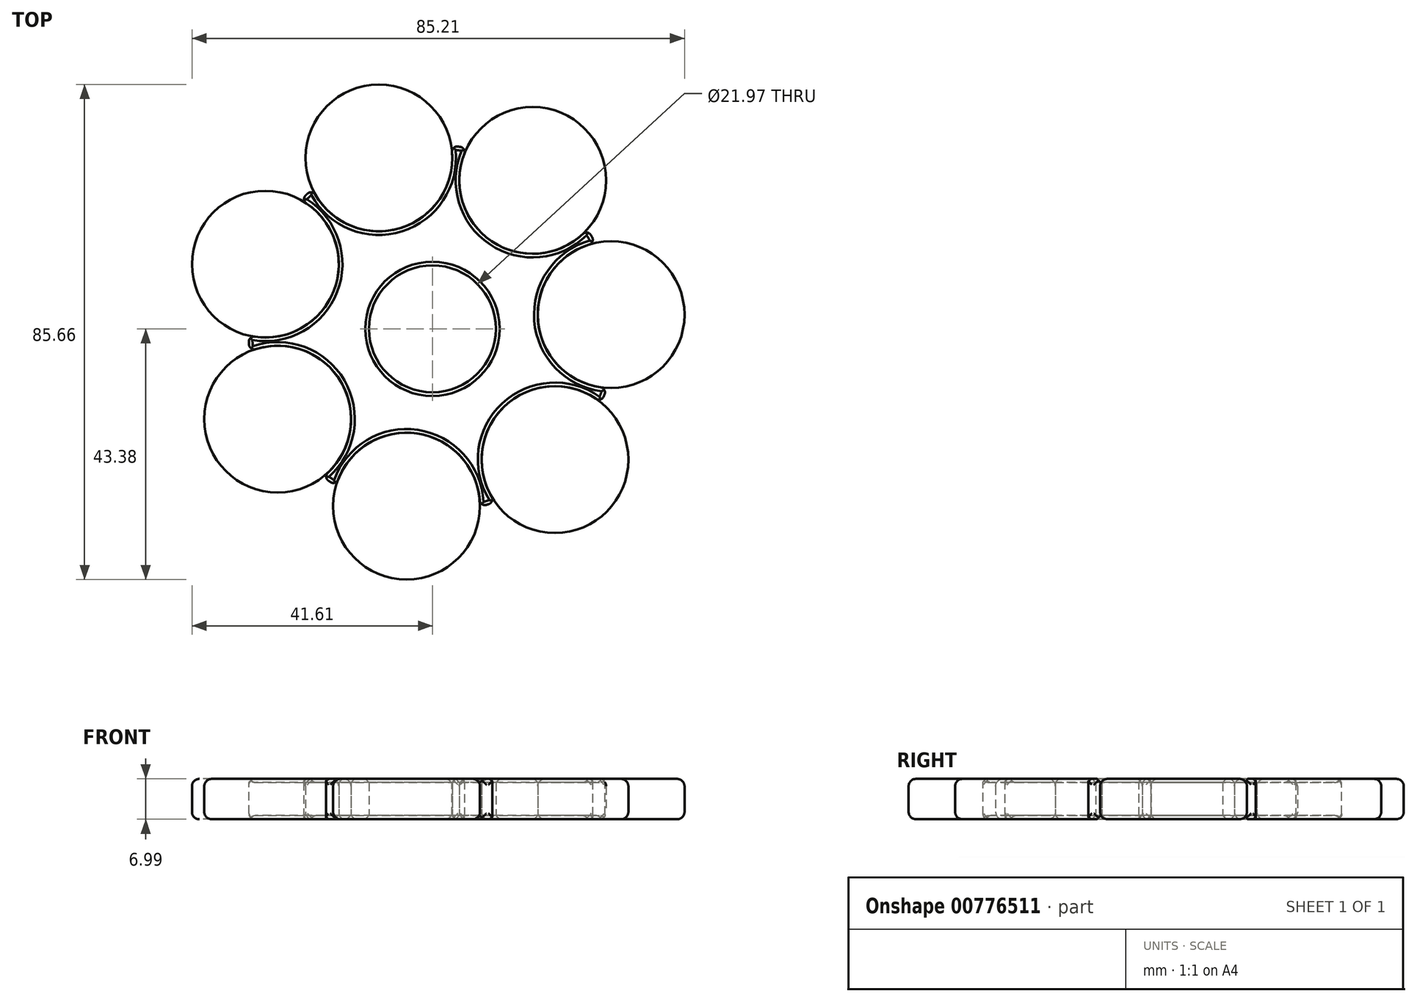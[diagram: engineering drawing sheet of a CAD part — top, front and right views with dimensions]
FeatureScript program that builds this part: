
annotation { "Feature Type Name" : "Feature", "Feature Type Description" : "" }
export const myFeature = defineFeature(function(context is Context, id is Id, definition is map)
    precondition{}
    {
        {
            var Q0;
            Q0=qCreatedBy(makeId("Top.planeOp"),FACE);
            var sketch = newSketch(context, id + "F0", { "sketchPlane" : qUnion([Q0])});
            skCircle(sketch, "E0", {"center": v(0, 0) * mm, "radius": 10.99 * mm});
            skCircle(sketch, "E1", {"center": v(0, 0) * mm, "radius": 15.88 * mm});
            skCircle(sketch, "E2.cCircle", {"center": v(0, 0) * mm, "radius": 27.93 * mm, "construction": true});
            skLineSegment(sketch, "E2.0", {"start": v(17.35, 25.7) * mm, "end": v(30.9, 2.46) * mm});
            skLineSegment(sketch, "E2.1", {"start": v(30.9, 2.46) * mm, "end": v(21.19, -22.63) * mm});
            skLineSegment(sketch, "E2.2", {"start": v(21.19, -22.63) * mm, "end": v(-4.48, -30.68) * mm});
            skLineSegment(sketch, "E2.3", {"start": v(-4.48, -30.68) * mm, "end": v(-26.78, -15.62) * mm});
            skLineSegment(sketch, "E2.4", {"start": v(-26.78, -15.62) * mm, "end": v(-28.9, 11.2) * mm});
            skLineSegment(sketch, "E2.5", {"start": v(-28.9, 11.2) * mm, "end": v(-9.27, 29.58) * mm});
            skLineSegment(sketch, "E2.6", {"start": v(-9.27, 29.58) * mm, "end": v(17.35, 25.7) * mm});
            skPoint(sketch, "E2.0.midPoint", {"position": v(24.13, 14.07) * mm});
            skCircle(sketch, "E3", {"center": v(17.35, 25.7) * mm, "radius": 12.7 * mm});
            skCircle(sketch, "E4", {"center": v(-9.27, 29.58) * mm, "radius": 12.7 * mm});
            skCircle(sketch, "E5", {"center": v(-28.9, 11.2) * mm, "radius": 12.7 * mm});
            skCircle(sketch, "E6", {"center": v(-26.78, -15.62) * mm, "radius": 12.7 * mm});
            skCircle(sketch, "E7", {"center": v(-4.48, -30.68) * mm, "radius": 12.7 * mm});
            skCircle(sketch, "E8", {"center": v(21.19, -22.63) * mm, "radius": 12.7 * mm});
            skCircle(sketch, "E9", {"center": v(30.9, 2.46) * mm, "radius": 12.7 * mm});
            skCircle(sketch, "E10", {"center": v(0, 0) * mm, "radius": 31.85 * mm});
            skCircle(sketch, "E11", {"center": v(0, 0) * mm, "radius": 23.5 * mm});
            skSolve(sketch);
        }
        {
            var Q0;
            {var subQ0=sQuery(id+"F0.wireOp",EDGE,"E10");var subQ1=sQuery(id+"F0.wireOp",EDGE,"E5");var subQ2=makeQuery(id+"F0.imprint","INTERSECT",VERTEX,{"disambiguationData":[OD(0.0)],"derivedFrom":[subQ1,subQ0]});Q0=makeQuery(id+"F0.imprint","IMPRINT",FACE,{"disambiguationData":[TD([[makeQuery(id+"F0.imprint","IMPRINT",EDGE,{"disambiguationData":[TD([[subQ2,-1.0]])],"derivedFrom":subQ1}),1.0]])]});}
            var Q1;
            {var subQ1=sQuery(id+"F0.wireOp",EDGE,"E2.4");var subQ5=sQuery(id+"F0.wireOp",EDGE,"E2.5");var subQ6=makeQuery(id+"F0.imprint","INTERSECT",VERTEX,{"derivedFrom":[subQ1,subQ5]});Q1=makeQuery(id+"F0.imprint","IMPRINT",FACE,{"disambiguationData":[TD([[makeQuery(id+"F0.imprint","IMPRINT",EDGE,{"disambiguationData":[TD([[subQ6,1.0]])],"derivedFrom":subQ1}),-1.0]])]});}
            var Q2;
            {var subQ0=sQuery(id+"F0.wireOp",EDGE,"E11");var subQ1=sQuery(id+"F0.wireOp",EDGE,"E5");var subQ2=makeQuery(id+"F0.imprint","INTERSECT",VERTEX,{"disambiguationData":[OD(0.0)],"derivedFrom":[subQ1,subQ0]});Q2=makeQuery(id+"F0.imprint","IMPRINT",FACE,{"disambiguationData":[TD([[makeQuery(id+"F0.imprint","IMPRINT",EDGE,{"disambiguationData":[TD([[subQ2,1.0]])],"derivedFrom":subQ1}),1.0]])]});}
            var Q3;
            {var subQ0=sQuery(id+"F0.wireOp",EDGE,"E11");var subQ1=sQuery(id+"F0.wireOp",EDGE,"E4");var subQ2=makeQuery(id+"F0.imprint","INTERSECT",VERTEX,{"disambiguationData":[OD(0.0)],"derivedFrom":[subQ1,subQ0]});Q3=makeQuery(id+"F0.imprint","IMPRINT",FACE,{"disambiguationData":[TD([[makeQuery(id+"F0.imprint","IMPRINT",EDGE,{"disambiguationData":[TD([[subQ2,-1.0]])],"derivedFrom":subQ1}),1.0]])]});}
            var Q4;
            {var subQ0=sQuery(id+"F0.wireOp",EDGE,"E10");var subQ1=sQuery(id+"F0.wireOp",EDGE,"E4");var subQ2=makeQuery(id+"F0.imprint","INTERSECT",VERTEX,{"disambiguationData":[OD(0.0)],"derivedFrom":[subQ1,subQ0]});Q4=makeQuery(id+"F0.imprint","IMPRINT",FACE,{"disambiguationData":[TD([[makeQuery(id+"F0.imprint","IMPRINT",EDGE,{"disambiguationData":[TD([[subQ2,1.0]])],"derivedFrom":subQ1}),1.0]])]});}
            var Q5;
            {var subQ0=sQuery(id+"F0.wireOp",EDGE,"E11");var subQ1=sQuery(id+"F0.wireOp",EDGE,"E3");var subQ2=makeQuery(id+"F0.imprint","INTERSECT",VERTEX,{"disambiguationData":[OD(0.0)],"derivedFrom":[subQ1,subQ0]});Q5=makeQuery(id+"F0.imprint","IMPRINT",FACE,{"disambiguationData":[TD([[makeQuery(id+"F0.imprint","IMPRINT",EDGE,{"disambiguationData":[TD([[subQ2,-1.0]])],"derivedFrom":subQ1}),1.0]])]});}
            var Q6;
            {var subQ0=sQuery(id+"F0.wireOp",EDGE,"E10");var subQ1=sQuery(id+"F0.wireOp",EDGE,"E3");var subQ2=makeQuery(id+"F0.imprint","INTERSECT",VERTEX,{"disambiguationData":[OD(0.0)],"derivedFrom":[subQ1,subQ0]});Q6=makeQuery(id+"F0.imprint","IMPRINT",FACE,{"disambiguationData":[TD([[makeQuery(id+"F0.imprint","IMPRINT",EDGE,{"disambiguationData":[TD([[subQ2,1.0]])],"derivedFrom":subQ1}),1.0]])]});}
            var Q7;
            {var subQ0=sQuery(id+"F0.wireOp",EDGE,"E10");var subQ1=sQuery(id+"F0.wireOp",EDGE,"E7");var subQ2=makeQuery(id+"F0.imprint","INTERSECT",VERTEX,{"disambiguationData":[OD(0.0)],"derivedFrom":[subQ1,subQ0]});Q7=makeQuery(id+"F0.imprint","IMPRINT",FACE,{"disambiguationData":[TD([[makeQuery(id+"F0.imprint","IMPRINT",EDGE,{"disambiguationData":[TD([[subQ2,-1.0]])],"derivedFrom":subQ1}),1.0]])]});}
            var Q8;
            {var subQ3=sQuery(id+"F0.wireOp",EDGE,"E2.2");var subQ6=sQuery(id+"F0.wireOp",EDGE,"E2.3");var subQ7=makeQuery(id+"F0.imprint","INTERSECT",VERTEX,{"derivedFrom":[subQ3,subQ6]});Q8=makeQuery(id+"F0.imprint","IMPRINT",FACE,{"disambiguationData":[TD([[makeQuery(id+"F0.imprint","IMPRINT",EDGE,{"disambiguationData":[TD([[subQ7,1.0]])],"derivedFrom":subQ3}),1.0]])]});}
            var Q9;
            {var subQ0=sQuery(id+"F0.wireOp",EDGE,"E11");var subQ1=sQuery(id+"F0.wireOp",EDGE,"E7");var subQ2=makeQuery(id+"F0.imprint","INTERSECT",VERTEX,{"disambiguationData":[OD(0.0)],"derivedFrom":[subQ1,subQ0]});Q9=makeQuery(id+"F0.imprint","IMPRINT",FACE,{"disambiguationData":[TD([[makeQuery(id+"F0.imprint","IMPRINT",EDGE,{"disambiguationData":[TD([[subQ2,-1.0]])],"derivedFrom":subQ1}),1.0]])]});}
            var Q10;
            {var subQ1=sQuery(id+"F0.wireOp",EDGE,"E2.3");var subQ5=sQuery(id+"F0.wireOp",EDGE,"E2.2");var subQ8=makeQuery(id+"F0.imprint","INTERSECT",VERTEX,{"derivedFrom":[subQ5,subQ1]});Q10=makeQuery(id+"F0.imprint","IMPRINT",FACE,{"disambiguationData":[TD([[makeQuery(id+"F0.imprint","IMPRINT",EDGE,{"disambiguationData":[TD([[subQ8,1.0]])],"derivedFrom":subQ5}),-1.0]])]});}
            var Q11;
            {var subQ0=sQuery(id+"F0.wireOp",EDGE,"E11");var subQ1=sQuery(id+"F0.wireOp",EDGE,"E6");var subQ2=makeQuery(id+"F0.imprint","INTERSECT",VERTEX,{"disambiguationData":[OD(0.0)],"derivedFrom":[subQ1,subQ0]});Q11=makeQuery(id+"F0.imprint","IMPRINT",FACE,{"disambiguationData":[TD([[makeQuery(id+"F0.imprint","IMPRINT",EDGE,{"disambiguationData":[TD([[subQ2,1.0]])],"derivedFrom":subQ1}),1.0]])]});}
            var Q12;
            {var subQ1=sQuery(id+"F0.wireOp",EDGE,"E2.3");var subQ5=sQuery(id+"F0.wireOp",EDGE,"E2.4");var subQ8=makeQuery(id+"F0.imprint","INTERSECT",VERTEX,{"derivedFrom":[subQ1,subQ5]});Q12=makeQuery(id+"F0.imprint","IMPRINT",FACE,{"disambiguationData":[TD([[makeQuery(id+"F0.imprint","IMPRINT",EDGE,{"disambiguationData":[TD([[subQ8,1.0]])],"derivedFrom":subQ1}),-1.0]])]});}
            var Q13;
            {var subQ3=sQuery(id+"F0.wireOp",EDGE,"E2.4");var subQ6=sQuery(id+"F0.wireOp",EDGE,"E2.3");var subQ8=makeQuery(id+"F0.imprint","INTERSECT",VERTEX,{"derivedFrom":[subQ6,subQ3]});Q13=makeQuery(id+"F0.imprint","IMPRINT",FACE,{"disambiguationData":[TD([[makeQuery(id+"F0.imprint","IMPRINT",EDGE,{"disambiguationData":[TD([[subQ8,1.0]])],"derivedFrom":subQ6}),1.0]])]});}
            var Q14;
            {var subQ0=sQuery(id+"F0.wireOp",EDGE,"E10");var subQ1=sQuery(id+"F0.wireOp",EDGE,"E6");var subQ2=makeQuery(id+"F0.imprint","INTERSECT",VERTEX,{"disambiguationData":[OD(0.0)],"derivedFrom":[subQ1,subQ0]});Q14=makeQuery(id+"F0.imprint","IMPRINT",FACE,{"disambiguationData":[TD([[makeQuery(id+"F0.imprint","IMPRINT",EDGE,{"disambiguationData":[TD([[subQ2,-1.0]])],"derivedFrom":subQ1}),1.0]])]});}
            var Q15;
            {var subQ0=sQuery(id+"F0.wireOp",EDGE,"E11");var subQ1=sQuery(id+"F0.wireOp",EDGE,"E8");var subQ2=makeQuery(id+"F0.imprint","INTERSECT",VERTEX,{"disambiguationData":[OD(0.0)],"derivedFrom":[subQ1,subQ0]});Q15=makeQuery(id+"F0.imprint","IMPRINT",FACE,{"disambiguationData":[TD([[makeQuery(id+"F0.imprint","IMPRINT",EDGE,{"disambiguationData":[TD([[subQ2,-1.0]])],"derivedFrom":subQ1}),1.0]])]});}
            var Q16;
            {var subQ1=sQuery(id+"F0.wireOp",EDGE,"E2.2");var subQ5=sQuery(id+"F0.wireOp",EDGE,"E2.1");var subQ8=makeQuery(id+"F0.imprint","INTERSECT",VERTEX,{"derivedFrom":[subQ5,subQ1]});Q16=makeQuery(id+"F0.imprint","IMPRINT",FACE,{"disambiguationData":[TD([[makeQuery(id+"F0.imprint","IMPRINT",EDGE,{"disambiguationData":[TD([[subQ8,1.0]])],"derivedFrom":subQ5}),-1.0]])]});}
            var Q17;
            {var subQ3=sQuery(id+"F0.wireOp",EDGE,"E2.1");var subQ5=sQuery(id+"F0.wireOp",EDGE,"E2.2");var subQ6=makeQuery(id+"F0.imprint","INTERSECT",VERTEX,{"derivedFrom":[subQ3,subQ5]});Q17=makeQuery(id+"F0.imprint","IMPRINT",FACE,{"disambiguationData":[TD([[makeQuery(id+"F0.imprint","IMPRINT",EDGE,{"disambiguationData":[TD([[subQ6,1.0]])],"derivedFrom":subQ3}),1.0]])]});}
            var Q18;
            {var subQ0=sQuery(id+"F0.wireOp",EDGE,"E10");var subQ1=sQuery(id+"F0.wireOp",EDGE,"E8");var subQ2=makeQuery(id+"F0.imprint","INTERSECT",VERTEX,{"disambiguationData":[OD(0.0)],"derivedFrom":[subQ1,subQ0]});Q18=makeQuery(id+"F0.imprint","IMPRINT",FACE,{"disambiguationData":[TD([[makeQuery(id+"F0.imprint","IMPRINT",EDGE,{"disambiguationData":[TD([[subQ2,1.0]])],"derivedFrom":subQ1}),1.0]])]});}
            var Q19;
            {var subQ0=sQuery(id+"F0.wireOp",EDGE,"E11");var subQ1=sQuery(id+"F0.wireOp",EDGE,"E9");var subQ2=makeQuery(id+"F0.imprint","INTERSECT",VERTEX,{"disambiguationData":[OD(0.0)],"derivedFrom":[subQ1,subQ0]});Q19=makeQuery(id+"F0.imprint","IMPRINT",FACE,{"disambiguationData":[TD([[makeQuery(id+"F0.imprint","IMPRINT",EDGE,{"disambiguationData":[TD([[subQ2,-1.0]])],"derivedFrom":subQ1}),1.0]])]});}
            var Q20;
            {var subQ1=sQuery(id+"F0.wireOp",EDGE,"E2.1");var subQ5=sQuery(id+"F0.wireOp",EDGE,"E2.0");var subQ8=makeQuery(id+"F0.imprint","INTERSECT",VERTEX,{"derivedFrom":[subQ5,subQ1]});Q20=makeQuery(id+"F0.imprint","IMPRINT",FACE,{"disambiguationData":[TD([[makeQuery(id+"F0.imprint","IMPRINT",EDGE,{"disambiguationData":[TD([[subQ8,1.0]])],"derivedFrom":subQ5}),-1.0]])]});}
            var Q21;
            {var subQ3=sQuery(id+"F0.wireOp",EDGE,"E2.1");var subQ5=sQuery(id+"F0.wireOp",EDGE,"E2.0");var subQ6=makeQuery(id+"F0.imprint","INTERSECT",VERTEX,{"derivedFrom":[subQ5,subQ3]});Q21=makeQuery(id+"F0.imprint","IMPRINT",FACE,{"disambiguationData":[TD([[makeQuery(id+"F0.imprint","IMPRINT",EDGE,{"disambiguationData":[TD([[subQ6,1.0]])],"derivedFrom":subQ5}),1.0]])]});}
            var Q22;
            {var subQ0=sQuery(id+"F0.wireOp",EDGE,"E10");var subQ1=sQuery(id+"F0.wireOp",EDGE,"E9");var subQ2=makeQuery(id+"F0.imprint","INTERSECT",VERTEX,{"disambiguationData":[OD(0.0)],"derivedFrom":[subQ1,subQ0]});Q22=makeQuery(id+"F0.imprint","IMPRINT",FACE,{"disambiguationData":[TD([[makeQuery(id+"F0.imprint","IMPRINT",EDGE,{"disambiguationData":[TD([[subQ2,1.0]])],"derivedFrom":subQ1}),1.0]])]});}
            var Q23;
            {var subQ3=sQuery(id+"F0.wireOp",EDGE,"E2.4");var subQ5=sQuery(id+"F0.wireOp",EDGE,"E2.5");var subQ6=makeQuery(id+"F0.imprint","INTERSECT",VERTEX,{"derivedFrom":[subQ3,subQ5]});Q23=makeQuery(id+"F0.imprint","IMPRINT",FACE,{"disambiguationData":[TD([[makeQuery(id+"F0.imprint","IMPRINT",EDGE,{"disambiguationData":[TD([[subQ6,1.0]])],"derivedFrom":subQ3}),1.0]])]});}
            var Q24;
            {var subQ6=sQuery(id+"F0.wireOp",EDGE,"E4");var subQ8=sQuery(id+"F0.wireOp",EDGE,"E2.5");var subQ9=makeQuery(id+"F0.imprint","INTERSECT",VERTEX,{"derivedFrom":[subQ8,subQ6]});Q24=makeQuery(id+"F0.imprint","IMPRINT",FACE,{"disambiguationData":[TD([[makeQuery(id+"F0.imprint","IMPRINT",EDGE,{"disambiguationData":[TD([[subQ9,-1.0]])],"derivedFrom":subQ8}),1.0]])]});}
            var Q25;
            {var subQ0=sQuery(id+"F0.wireOp",EDGE,"E4");var subQ5=sQuery(id+"F0.wireOp",EDGE,"E2.5");var subQ6=makeQuery(id+"F0.imprint","INTERSECT",VERTEX,{"derivedFrom":[subQ5,subQ0]});Q25=makeQuery(id+"F0.imprint","IMPRINT",FACE,{"disambiguationData":[TD([[makeQuery(id+"F0.imprint","IMPRINT",EDGE,{"disambiguationData":[TD([[subQ6,-1.0]])],"derivedFrom":subQ5}),-1.0]])]});}
            var Q26;
            {var subQ1=sQuery(id+"F0.wireOp",EDGE,"E2.6");var subQ6=sQuery(id+"F0.wireOp",EDGE,"E3");var subQ9=makeQuery(id+"F0.imprint","INTERSECT",VERTEX,{"derivedFrom":[subQ1,subQ6]});Q26=makeQuery(id+"F0.imprint","IMPRINT",FACE,{"disambiguationData":[TD([[makeQuery(id+"F0.imprint","IMPRINT",EDGE,{"disambiguationData":[TD([[subQ9,-1.0]])],"derivedFrom":subQ1}),1.0]])]});}
            var Q27;
            {var subQ1=sQuery(id+"F0.wireOp",EDGE,"E2.6");var subQ5=sQuery(id+"F0.wireOp",EDGE,"E2.0");var subQ6=makeQuery(id+"F0.imprint","INTERSECT",VERTEX,{"derivedFrom":[subQ5,subQ1]});Q27=makeQuery(id+"F0.imprint","IMPRINT",FACE,{"disambiguationData":[TD([[makeQuery(id+"F0.imprint","IMPRINT",EDGE,{"disambiguationData":[TD([[subQ6,-1.0]])],"derivedFrom":subQ5}),-1.0]])]});}
            var Q28;
            {var subQ3=sQuery(id+"F0.wireOp",EDGE,"E2.0");var subQ5=sQuery(id+"F0.wireOp",EDGE,"E2.6");var subQ6=makeQuery(id+"F0.imprint","INTERSECT",VERTEX,{"derivedFrom":[subQ3,subQ5]});Q28=makeQuery(id+"F0.imprint","IMPRINT",FACE,{"disambiguationData":[TD([[makeQuery(id+"F0.imprint","IMPRINT",EDGE,{"disambiguationData":[TD([[subQ6,-1.0]])],"derivedFrom":subQ3}),1.0]])]});}
            extrude(context, id + "F1", {"entities" : qUnion([Q0, Q1, Q2, Q3, Q4, Q5, Q6, Q7, Q8, Q9, Q10, Q11, Q12, Q13, Q14, Q15, Q16, Q17, Q18, Q19, Q20, Q21, Q22, Q23, Q24, Q25, Q26, Q27, Q28]), "depth" : 7 * mm, "offsetDistance" : 25.4 * mm});
        }
        {
            var Q0;
            Q0=makeQuery(id+"F0.imprint","IMPRINT",FACE,{"disambiguationData":[TD([[makeQuery(id+"F0.imprint","IMPRINT",EDGE,{"derivedFrom":sQuery(id+"F0.wireOp",EDGE,"E1")}),-1.0]])]});
            var Q1;
            Q1=makeQuery(id+"F0.imprint","IMPRINT",FACE,{"disambiguationData":[TD([[makeQuery(id+"F0.imprint","IMPRINT",EDGE,{"derivedFrom":sQuery(id+"F0.wireOp",EDGE,"E0")}),-1.0]])]});
            var Q2;
            {var subQ0=sQuery(id+"F0.wireOp",EDGE,"E5");var subQ1=sQuery(id+"F0.wireOp",EDGE,"E2.5");var subQ2=makeQuery(id+"F0.imprint","INTERSECT",VERTEX,{"derivedFrom":[subQ1,subQ0]});Q2=makeQuery(id+"F0.imprint","IMPRINT",FACE,{"disambiguationData":[TD([[makeQuery(id+"F0.imprint","IMPRINT",EDGE,{"disambiguationData":[TD([[subQ2,-1.0]])],"derivedFrom":subQ1}),-1.0]])]});}
            var Q3;
            {var subQ0=sQuery(id+"F0.wireOp",EDGE,"E5");var subQ1=sQuery(id+"F0.wireOp",EDGE,"E2.5");var subQ2=makeQuery(id+"F0.imprint","INTERSECT",VERTEX,{"derivedFrom":[subQ1,subQ0]});Q3=makeQuery(id+"F0.imprint","IMPRINT",FACE,{"disambiguationData":[TD([[makeQuery(id+"F0.imprint","IMPRINT",EDGE,{"disambiguationData":[TD([[subQ2,-1.0]])],"derivedFrom":subQ1}),1.0]])]});}
            var Q4;
            {var subQ0=sQuery(id+"F0.wireOp",EDGE,"E6");var subQ1=sQuery(id+"F0.wireOp",EDGE,"E2.4");var subQ2=makeQuery(id+"F0.imprint","INTERSECT",VERTEX,{"derivedFrom":[subQ1,subQ0]});Q4=makeQuery(id+"F0.imprint","IMPRINT",FACE,{"disambiguationData":[TD([[makeQuery(id+"F0.imprint","IMPRINT",EDGE,{"disambiguationData":[TD([[subQ2,-1.0]])],"derivedFrom":subQ1}),-1.0]])]});}
            var Q5;
            {var subQ0=sQuery(id+"F0.wireOp",EDGE,"E6");var subQ1=sQuery(id+"F0.wireOp",EDGE,"E2.4");var subQ2=makeQuery(id+"F0.imprint","INTERSECT",VERTEX,{"derivedFrom":[subQ1,subQ0]});Q5=makeQuery(id+"F0.imprint","IMPRINT",FACE,{"disambiguationData":[TD([[makeQuery(id+"F0.imprint","IMPRINT",EDGE,{"disambiguationData":[TD([[subQ2,-1.0]])],"derivedFrom":subQ1}),1.0]])]});}
            var Q6;
            {var subQ0=sQuery(id+"F0.wireOp",EDGE,"E7");var subQ1=sQuery(id+"F0.wireOp",EDGE,"E2.3");var subQ2=makeQuery(id+"F0.imprint","INTERSECT",VERTEX,{"derivedFrom":[subQ1,subQ0]});Q6=makeQuery(id+"F0.imprint","IMPRINT",FACE,{"disambiguationData":[TD([[makeQuery(id+"F0.imprint","IMPRINT",EDGE,{"disambiguationData":[TD([[subQ2,-1.0]])],"derivedFrom":subQ1}),-1.0]])]});}
            var Q7;
            {var subQ0=sQuery(id+"F0.wireOp",EDGE,"E7");var subQ1=sQuery(id+"F0.wireOp",EDGE,"E2.3");var subQ2=makeQuery(id+"F0.imprint","INTERSECT",VERTEX,{"derivedFrom":[subQ1,subQ0]});Q7=makeQuery(id+"F0.imprint","IMPRINT",FACE,{"disambiguationData":[TD([[makeQuery(id+"F0.imprint","IMPRINT",EDGE,{"disambiguationData":[TD([[subQ2,-1.0]])],"derivedFrom":subQ1}),1.0]])]});}
            var Q8;
            {var subQ0=sQuery(id+"F0.wireOp",EDGE,"E8");var subQ1=sQuery(id+"F0.wireOp",EDGE,"E2.2");var subQ2=makeQuery(id+"F0.imprint","INTERSECT",VERTEX,{"derivedFrom":[subQ1,subQ0]});Q8=makeQuery(id+"F0.imprint","IMPRINT",FACE,{"disambiguationData":[TD([[makeQuery(id+"F0.imprint","IMPRINT",EDGE,{"disambiguationData":[TD([[subQ2,-1.0]])],"derivedFrom":subQ1}),-1.0]])]});}
            var Q9;
            {var subQ0=sQuery(id+"F0.wireOp",EDGE,"E8");var subQ1=sQuery(id+"F0.wireOp",EDGE,"E2.2");var subQ2=makeQuery(id+"F0.imprint","INTERSECT",VERTEX,{"derivedFrom":[subQ1,subQ0]});Q9=makeQuery(id+"F0.imprint","IMPRINT",FACE,{"disambiguationData":[TD([[makeQuery(id+"F0.imprint","IMPRINT",EDGE,{"disambiguationData":[TD([[subQ2,-1.0]])],"derivedFrom":subQ1}),1.0]])]});}
            var Q10;
            {var subQ0=sQuery(id+"F0.wireOp",EDGE,"E9");var subQ1=sQuery(id+"F0.wireOp",EDGE,"E2.1");var subQ2=makeQuery(id+"F0.imprint","INTERSECT",VERTEX,{"derivedFrom":[subQ1,subQ0]});Q10=makeQuery(id+"F0.imprint","IMPRINT",FACE,{"disambiguationData":[TD([[makeQuery(id+"F0.imprint","IMPRINT",EDGE,{"disambiguationData":[TD([[subQ2,-1.0]])],"derivedFrom":subQ1}),-1.0]])]});}
            var Q11;
            {var subQ0=sQuery(id+"F0.wireOp",EDGE,"E9");var subQ1=sQuery(id+"F0.wireOp",EDGE,"E2.1");var subQ2=makeQuery(id+"F0.imprint","INTERSECT",VERTEX,{"derivedFrom":[subQ1,subQ0]});Q11=makeQuery(id+"F0.imprint","IMPRINT",FACE,{"disambiguationData":[TD([[makeQuery(id+"F0.imprint","IMPRINT",EDGE,{"disambiguationData":[TD([[subQ2,-1.0]])],"derivedFrom":subQ1}),1.0]])]});}
            var Q12;
            {var subQ0=sQuery(id+"F0.wireOp",EDGE,"E4");var subQ1=sQuery(id+"F0.wireOp",EDGE,"E2.6");var subQ2=makeQuery(id+"F0.imprint","INTERSECT",VERTEX,{"derivedFrom":[subQ1,subQ0]});Q12=makeQuery(id+"F0.imprint","IMPRINT",FACE,{"disambiguationData":[TD([[makeQuery(id+"F0.imprint","IMPRINT",EDGE,{"disambiguationData":[TD([[subQ2,-1.0]])],"derivedFrom":subQ1}),-1.0]])]});}
            var Q13;
            {var subQ0=sQuery(id+"F0.wireOp",EDGE,"E4");var subQ1=sQuery(id+"F0.wireOp",EDGE,"E2.6");var subQ2=makeQuery(id+"F0.imprint","INTERSECT",VERTEX,{"derivedFrom":[subQ1,subQ0]});Q13=makeQuery(id+"F0.imprint","IMPRINT",FACE,{"disambiguationData":[TD([[makeQuery(id+"F0.imprint","IMPRINT",EDGE,{"disambiguationData":[TD([[subQ2,-1.0]])],"derivedFrom":subQ1}),1.0]])]});}
            var Q14;
            {var subQ0=sQuery(id+"F0.wireOp",EDGE,"E3");var subQ1=sQuery(id+"F0.wireOp",EDGE,"E2.0");var subQ2=makeQuery(id+"F0.imprint","INTERSECT",VERTEX,{"derivedFrom":[subQ1,subQ0]});Q14=makeQuery(id+"F0.imprint","IMPRINT",FACE,{"disambiguationData":[TD([[makeQuery(id+"F0.imprint","IMPRINT",EDGE,{"disambiguationData":[TD([[subQ2,-1.0]])],"derivedFrom":subQ1}),1.0]])]});}
            var Q15;
            {var subQ0=sQuery(id+"F0.wireOp",EDGE,"E3");var subQ1=sQuery(id+"F0.wireOp",EDGE,"E2.0");var subQ2=makeQuery(id+"F0.imprint","INTERSECT",VERTEX,{"derivedFrom":[subQ1,subQ0]});Q15=makeQuery(id+"F0.imprint","IMPRINT",FACE,{"disambiguationData":[TD([[makeQuery(id+"F0.imprint","IMPRINT",EDGE,{"disambiguationData":[TD([[subQ2,-1.0]])],"derivedFrom":subQ1}),-1.0]])]});}
            extrude(context, id + "F2", {"entities" : qUnion([Q0, Q1, Q2, Q3, Q4, Q5, Q6, Q7, Q8, Q9, Q10, Q11, Q12, Q13, Q14, Q15]), "depth" : 7 * mm, "offsetDistance" : 25.4 * mm});
        }
        {
            var Q0;
            Q0=makeQuery(id+"F2.opExtrude","CAP_FACE",FACE,{"disambiguationData":[OSD([sQuery(id+"F0.wireOp",EDGE,"E0"),sQuery(id+"F0.wireOp",EDGE,"E3"),sQuery(id+"F0.wireOp",EDGE,"E4"),sQuery(id+"F0.wireOp",EDGE,"E5"),sQuery(id+"F0.wireOp",EDGE,"E6"),sQuery(id+"F0.wireOp",EDGE,"E7"),sQuery(id+"F0.wireOp",EDGE,"E8"),sQuery(id+"F0.wireOp",EDGE,"E9"),sQuery(id+"F0.wireOp",EDGE,"E10")])],"isStart":false});
            var Q1;
            Q1=makeQuery(id+"F2.opExtrude","CAP_FACE",FACE,{"disambiguationData":[OSD([sQuery(id+"F0.wireOp",EDGE,"E0"),sQuery(id+"F0.wireOp",EDGE,"E3"),sQuery(id+"F0.wireOp",EDGE,"E4"),sQuery(id+"F0.wireOp",EDGE,"E5"),sQuery(id+"F0.wireOp",EDGE,"E6"),sQuery(id+"F0.wireOp",EDGE,"E7"),sQuery(id+"F0.wireOp",EDGE,"E8"),sQuery(id+"F0.wireOp",EDGE,"E9"),sQuery(id+"F0.wireOp",EDGE,"E10")])],"isStart":true});
            chamfer(context, id + "F3", {"entities" : qUnion([Q0, Q1]), "width" : 0.64 * mm, "tangentPropagation" : true});
        }
        {
            var Q0;
            {var subQ0=sQuery(id+"F0.wireOp",EDGE,"E10");Q0=makeQuery(id+"F2.opExtrude","SWEPT_FACE",FACE,{"disambiguationData":[OSD([subQ0]),TDD([makeQuery(id+"F0.imprint","IMPRINT",EDGE,{"disambiguationData":[TD([[makeQuery(id+"F0.imprint","INTERSECT",VERTEX,{"disambiguationData":[OD(0.0)],"derivedFrom":[sQuery(id+"F0.wireOp",EDGE,"E4"),subQ0]}),-1.0]])],"derivedFrom":subQ0})])]});}
            var Q1;
            {var subQ0=sQuery(id+"F0.wireOp",EDGE,"E10");Q1=makeQuery(id+"F2.opExtrude","SWEPT_FACE",FACE,{"disambiguationData":[OSD([subQ0]),TDD([makeQuery(id+"F0.imprint","IMPRINT",EDGE,{"disambiguationData":[TD([[makeQuery(id+"F0.imprint","INTERSECT",VERTEX,{"disambiguationData":[OD(1.0)],"derivedFrom":[sQuery(id+"F0.wireOp",EDGE,"E5"),subQ0]}),-1.0]])],"derivedFrom":subQ0})])]});}
            var Q2;
            {var subQ0=sQuery(id+"F0.wireOp",EDGE,"E10");Q2=makeQuery(id+"F2.opExtrude","SWEPT_FACE",FACE,{"disambiguationData":[OSD([subQ0]),TDD([makeQuery(id+"F0.imprint","IMPRINT",EDGE,{"disambiguationData":[TD([[makeQuery(id+"F0.imprint","INTERSECT",VERTEX,{"disambiguationData":[OD(1.0)],"derivedFrom":[sQuery(id+"F0.wireOp",EDGE,"E6"),subQ0]}),-1.0]])],"derivedFrom":subQ0})])]});}
            var Q3;
            {var subQ0=sQuery(id+"F0.wireOp",EDGE,"E10");Q3=makeQuery(id+"F2.opExtrude","SWEPT_FACE",FACE,{"disambiguationData":[OSD([subQ0]),TDD([makeQuery(id+"F0.imprint","IMPRINT",EDGE,{"disambiguationData":[TD([[makeQuery(id+"F0.imprint","INTERSECT",VERTEX,{"disambiguationData":[OD(0.0)],"derivedFrom":[sQuery(id+"F0.wireOp",EDGE,"E3"),subQ0]}),-1.0]])],"derivedFrom":subQ0})])]});}
            var Q4;
            {var subQ0=sQuery(id+"F0.wireOp",EDGE,"E10");Q4=makeQuery(id+"F2.opExtrude","SWEPT_FACE",FACE,{"disambiguationData":[OSD([subQ0]),TDD([makeQuery(id+"F0.imprint","IMPRINT",EDGE,{"disambiguationData":[TD([[makeQuery(id+"F0.imprint","INTERSECT",VERTEX,{"disambiguationData":[OD(1.0)],"derivedFrom":[sQuery(id+"F0.wireOp",EDGE,"E3"),subQ0]}),1.0]])],"derivedFrom":subQ0})])]});}
            var Q5;
            {var subQ0=sQuery(id+"F0.wireOp",EDGE,"E10");Q5=makeQuery(id+"F2.opExtrude","SWEPT_FACE",FACE,{"disambiguationData":[OSD([subQ0]),TDD([makeQuery(id+"F0.imprint","IMPRINT",EDGE,{"disambiguationData":[TD([[makeQuery(id+"F0.imprint","INTERSECT",VERTEX,{"disambiguationData":[OD(0.0)],"derivedFrom":[sQuery(id+"F0.wireOp",EDGE,"E8"),subQ0]}),-1.0]])],"derivedFrom":subQ0})])]});}
            var Q6;
            {var subQ0=sQuery(id+"F0.wireOp",EDGE,"E10");Q6=makeQuery(id+"F2.opExtrude","SWEPT_FACE",FACE,{"disambiguationData":[OSD([subQ0]),TDD([makeQuery(id+"F0.imprint","IMPRINT",EDGE,{"disambiguationData":[TD([[makeQuery(id+"F0.imprint","INTERSECT",VERTEX,{"disambiguationData":[OD(1.0)],"derivedFrom":[sQuery(id+"F0.wireOp",EDGE,"E7"),subQ0]}),-1.0]])],"derivedFrom":subQ0})])]});}
            fillet(context, id + "F4", {"entities" : qUnion([Q0, Q1, Q2, Q3, Q4, Q5, Q6]), "radius" : 0.89 * mm, "tangentPropagation" : true, "allowEdgeOverflow" : false});
        }
        {
            var Q0;
            Q0=makeQuery(id+"F1.opExtrude","CAP_EDGE",EDGE,{"disambiguationData":[OSD([sQuery(id+"F0.wireOp",EDGE,"E4")])],"isStart":false});
            var Q1;
            Q1=makeQuery(id+"F1.opExtrude","CAP_EDGE",EDGE,{"disambiguationData":[OSD([sQuery(id+"F0.wireOp",EDGE,"E3")])],"isStart":false});
            var Q2;
            Q2=makeQuery(id+"F1.opExtrude","CAP_EDGE",EDGE,{"disambiguationData":[OSD([sQuery(id+"F0.wireOp",EDGE,"E5")])],"isStart":false});
            var Q3;
            Q3=makeQuery(id+"F1.opExtrude","CAP_EDGE",EDGE,{"disambiguationData":[OSD([sQuery(id+"F0.wireOp",EDGE,"E9")])],"isStart":false});
            var Q4;
            Q4=makeQuery(id+"F1.opExtrude","CAP_EDGE",EDGE,{"disambiguationData":[OSD([sQuery(id+"F0.wireOp",EDGE,"E8")])],"isStart":false});
            var Q5;
            Q5=makeQuery(id+"F1.opExtrude","CAP_EDGE",EDGE,{"disambiguationData":[OSD([sQuery(id+"F0.wireOp",EDGE,"E7")])],"isStart":false});
            var Q6;
            Q6=makeQuery(id+"F1.opExtrude","CAP_EDGE",EDGE,{"disambiguationData":[OSD([sQuery(id+"F0.wireOp",EDGE,"E6")])],"isStart":false});
            var Q7;
            Q7=makeQuery(id+"F1.opExtrude","CAP_EDGE",EDGE,{"disambiguationData":[OSD([sQuery(id+"F0.wireOp",EDGE,"E8")])],"isStart":true});
            var Q8;
            Q8=makeQuery(id+"F1.opExtrude","CAP_EDGE",EDGE,{"disambiguationData":[OSD([sQuery(id+"F0.wireOp",EDGE,"E7")])],"isStart":true});
            var Q9;
            Q9=makeQuery(id+"F1.opExtrude","CAP_EDGE",EDGE,{"disambiguationData":[OSD([sQuery(id+"F0.wireOp",EDGE,"E6")])],"isStart":true});
            var Q10;
            Q10=makeQuery(id+"F1.opExtrude","CAP_EDGE",EDGE,{"disambiguationData":[OSD([sQuery(id+"F0.wireOp",EDGE,"E5")])],"isStart":true});
            var Q11;
            Q11=makeQuery(id+"F1.opExtrude","CAP_EDGE",EDGE,{"disambiguationData":[OSD([sQuery(id+"F0.wireOp",EDGE,"E4")])],"isStart":true});
            var Q12;
            Q12=makeQuery(id+"F1.opExtrude","CAP_EDGE",EDGE,{"disambiguationData":[OSD([sQuery(id+"F0.wireOp",EDGE,"E3")])],"isStart":true});
            var Q13;
            Q13=makeQuery(id+"F1.opExtrude","CAP_EDGE",EDGE,{"disambiguationData":[OSD([sQuery(id+"F0.wireOp",EDGE,"E9")])],"isStart":true});
            fillet(context, id + "F5", {"entities" : qUnion([Q0, Q1, Q2, Q3, Q4, Q5, Q6, Q7, Q8, Q9, Q10, Q11, Q12, Q13]), "radius" : 1.27 * mm, "tangentPropagation" : true, "allowEdgeOverflow" : false});
        }
    });
